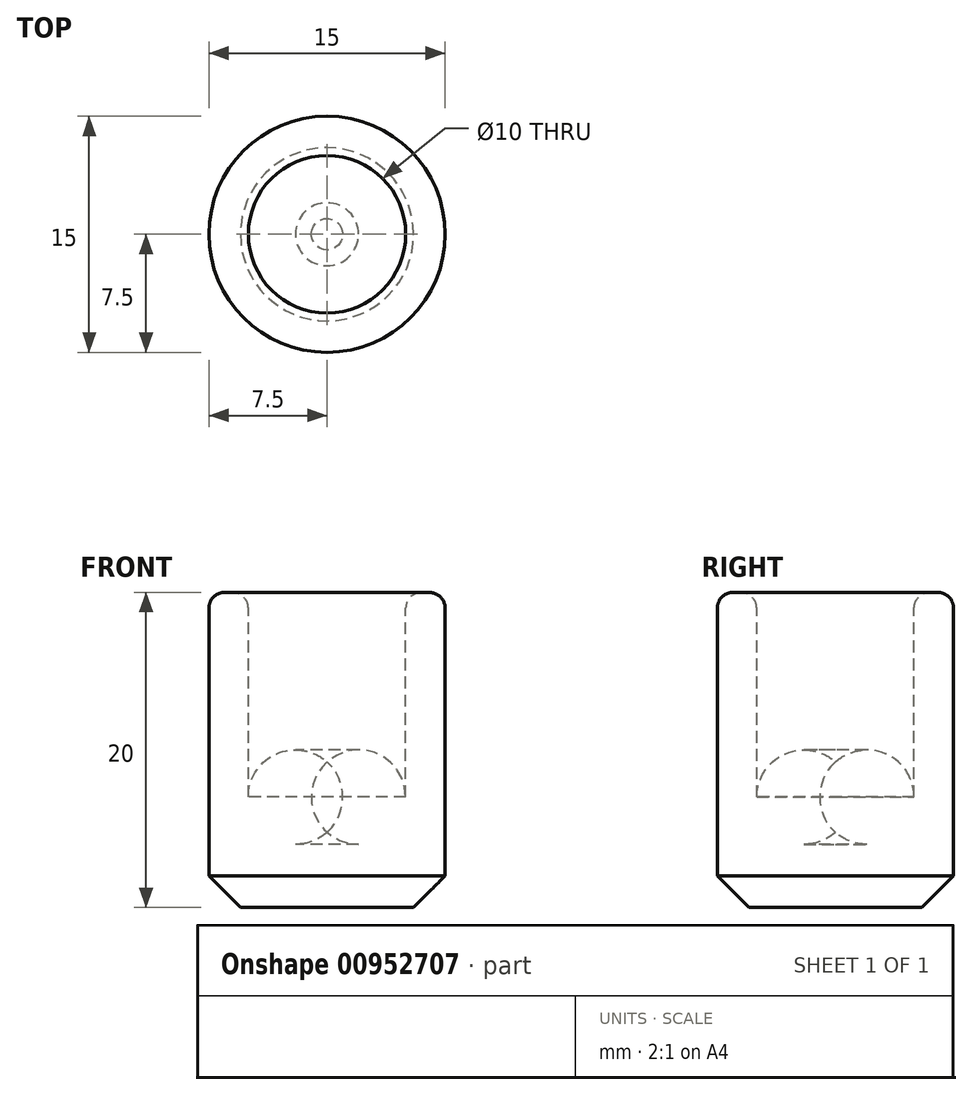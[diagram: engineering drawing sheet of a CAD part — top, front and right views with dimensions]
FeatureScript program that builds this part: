
annotation { "Feature Type Name" : "Feature", "Feature Type Description" : "" }
export const myFeature = defineFeature(function(context is Context, id is Id, definition is map)
    precondition{}
    {
        {
            var Q0;
            Q0=qCreatedBy(makeId("Top.planeOp"),FACE);
            var sketch = newSketch(context, id + "F0", { "sketchPlane" : qUnion([Q0])});
            skCircle(sketch, "E0", {"center": v(0, 0) * mm, "radius": 7.5 * mm});
            skSolve(sketch);
        }
        {
            var Q0;
            Q0=makeQuery(id+"F0.imprint","IMPRINT",FACE,{"disambiguationData":[TD([[makeQuery(id+"F0.imprint","IMPRINT",EDGE,{"derivedFrom":sQuery(id+"F0.wireOp",EDGE,"E0")}),1.0]])]});
            extrude(context, id + "F1", {"entities" : qUnion([Q0]), "depth" : 20 * mm, "offsetDistance" : 25 * mm});
        }
        {
            var Q0;
            Q0=makeQuery(id+"F1.opExtrude","CAP_FACE",FACE,{"disambiguationData":[OSD([sQuery(id+"F0.wireOp",EDGE,"E0")])],"isStart":false});
            var sketch = newSketch(context, id + "F2", { "sketchPlane" : qUnion([Q0])});
            skCircle(sketch, "E1", {"center": v(0, 0) * mm, "radius": 5 * mm});
            skSolve(sketch);
        }
        {
            var Q0;
            Q0=makeQuery(id+"F2.imprint","IMPRINT",FACE,{"disambiguationData":[TD([[makeQuery(id+"F2.imprint","IMPRINT",EDGE,{"derivedFrom":sQuery(id+"F2.wireOp",EDGE,"E1")}),1.0]])]});
            extrude(context, id + "F3", {"entities" : qUnion([Q0]), "operationType" : NewBodyOperationType.REMOVE, "oppositeDirection" : true, "depth" : 16 * mm, "offsetDistance" : 25 * mm});
        }
        {
            var Q0;
            Q0=makeQuery(id+"F1.opExtrude","CAP_EDGE",EDGE,{"disambiguationData":[OSD([sQuery(id+"F0.wireOp",EDGE,"E0")])],"isStart":true});
            chamfer(context, id + "F4", {"entities" : qUnion([Q0]), "width" : 2 * mm, "tangentPropagation" : true});
        }
        {
            var Q0;
            Q0=makeQuery(id+"F1.opExtrude","CAP_FACE",FACE,{"disambiguationData":[OSD([sQuery(id+"F0.wireOp",EDGE,"E0")])],"isStart":false});
            fillet(context, id + "F5", {"entities" : qUnion([Q0]), "radius" : 1 * mm, "tangentPropagation" : true, "allowEdgeOverflow" : false});
        }
        {
            var Q0;
            Q0=makeQuery(id+"F3.boolean.opBoolean","COPY",EDGE,{"derivedFrom":makeQuery(id+"F3.opExtrude","CAP_EDGE",EDGE,{"disambiguationData":[OSD([sQuery(id+"F2.wireOp",EDGE,"E1")])],"isStart":false})});
            fillet(context, id + "F6", {"entities" : qUnion([Q0]), "radius" : 3 * mm, "tangentPropagation" : true, "allowEdgeOverflow" : false});
        }
    });
